# Revit family: FU_Chair_Sandler_VARYA_1-2
name_source: partatom
category: Furniture
units: mm (PartAtom-declared; Revit-internal decimal feet)

## family parameters
Always vertical = No
Cut with Voids When Loaded = No
OmniClass Number = 23.21.23.15.17
Room Calculation Point = No
Shared = No
Work Plane-Based = Yes

## types (2) — shared parameters
401D = No
401G = No
BIMobject category = Chair
BIMobject category code = furniture-chair
BIMobject main category = Furniture
BIMobject main category code = furniture
Brand url = https://www.sandlerseating.com
Default Elevation = 1219.2 mm  [stored 4 ft]
Description = Chair
Design country = Brasil
Edition number = 1
Frame = BS02
Height Frame = 458.9 mm  [stored 1.50558 ft]
IFC Classification = Furnishing Element
Manufacturer = Sandler
Manufacturer country = USA
Manufacturer name = Sandler
Masterformat 2014 Code = 12 48 43.13
Masterformat 2014 Description = Chair Mats
OmniClass Code = 23-21 23 15 17
Product Guid = ??
Product SKU = ??
Product data url = https://www.sandlerseating.com
Product family = Furniture
Product group = Chair
QR code = https://www.sandlerseating.com
Uniformat II Description = Movable Furnishings

## per-type parameters (varying)
| type | Frame Material | Seat Material | Shell | Shell Material |
| VARYA 1.2 PP | M1_W01 - White | Fabric - Gravity - Wheat CPC21 | TP01 | M2_M38 |
| VARYA 1.2 | M1_B00 - Black | Fabric - Mainline Flax - Kensington MLF07 | TP02 | M1_W01 - White |

note: column(s) folded — value = type name in every type: Model, Product name

note: [stored X ft] marks values corroborated as IEEE doubles in the binary element streams (Revit-internal decimal feet)

## geometry (parser evidence)
native form markers: Sweep x24
no freeform markers — native parametric forms only
